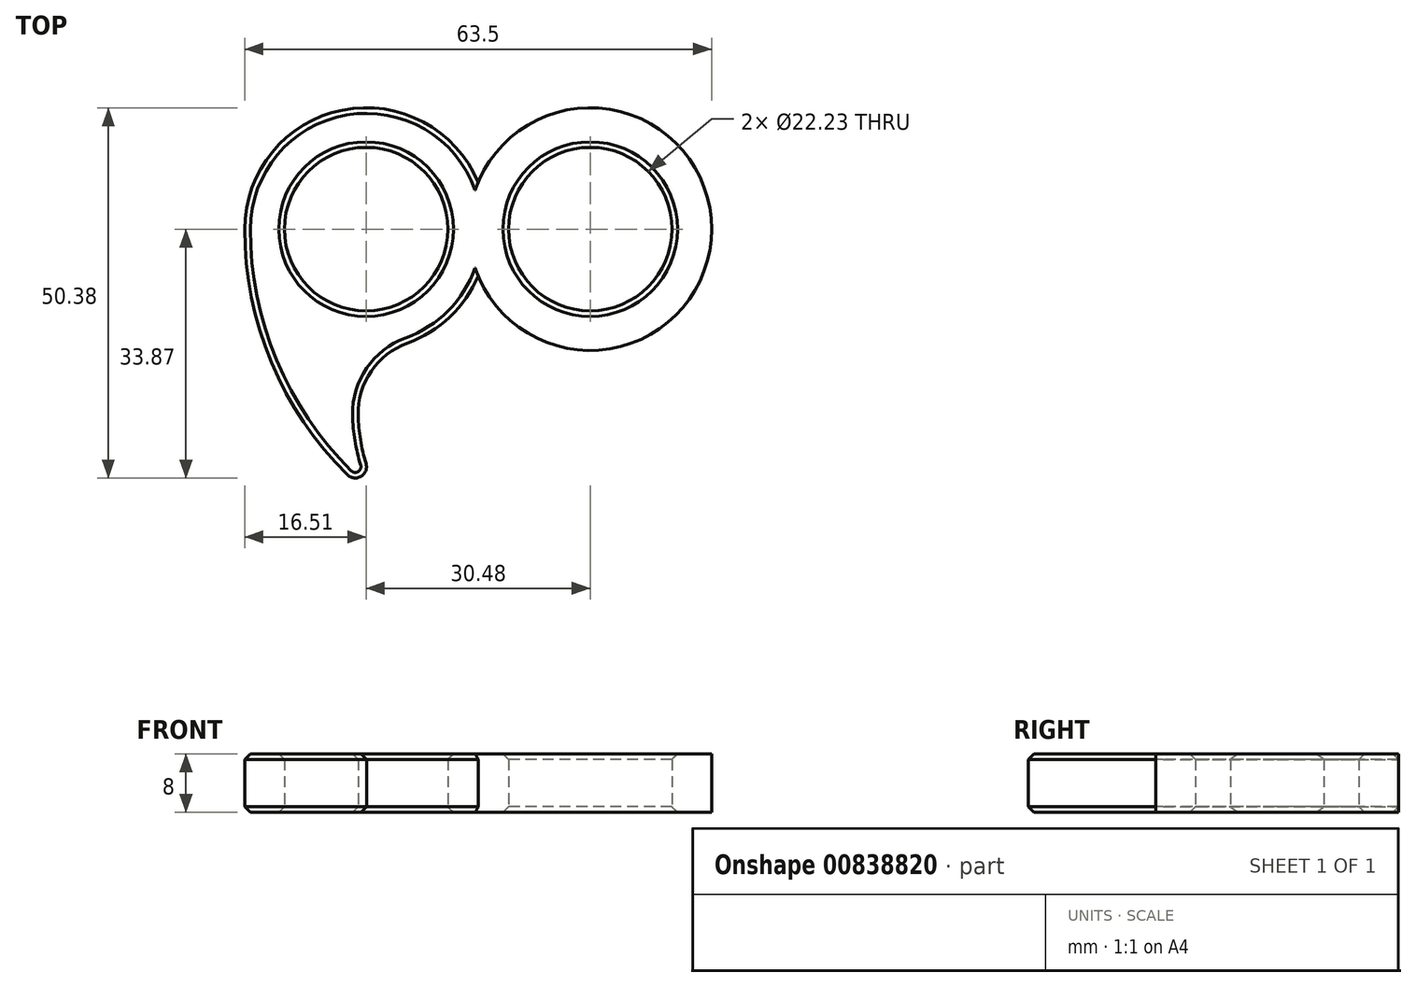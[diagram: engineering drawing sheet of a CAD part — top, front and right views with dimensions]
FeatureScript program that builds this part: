
annotation { "Feature Type Name" : "Feature", "Feature Type Description" : "" }
export const myFeature = defineFeature(function(context is Context, id is Id, definition is map)
    precondition{}
    {
        {
            var Q0;
            Q0=qCreatedBy(makeId("Top.planeOp"),FACE);
            var sketch = newSketch(context, id + "F0", { "sketchPlane" : qUnion([Q0])});
            skCircle(sketch, "E0", {"center": v(0, 0) * mm, "radius": 11.11 * mm});
            skCircle(sketch, "E1", {"center": v(0, 0) * mm, "radius": 16.51 * mm});
            skCircle(sketch, "E2", {"center": v(-30.48, 0) * mm, "radius": 11.11 * mm});
            skCircle(sketch, "E3", {"center": v(-30.48, 0) * mm, "radius": 16.51 * mm});
            skCircle(sketch, "E4", {"center": v(0, 0) * mm, "radius": 47 * mm});
            skArc(sketch, "E5", {"start": v(-30.15, -16.5) * mm, "mid": v(-31.4, -27.53) * mm, "end": v(-27.68, -37.97) * mm});
            skSolve(sketch);
        }
        {
            var Q0;
            Q0=makeQuery(id+"F0.imprint","IMPRINT",FACE,{"disambiguationData":[TD([[makeQuery(id+"F0.imprint","IMPRINT",EDGE,{"derivedFrom":sQuery(id+"F0.wireOp",EDGE,"E0")}),-1.0]])]});
            var Q1;
            {var subQ0=sQuery(id+"F0.wireOp",EDGE,"E3");var subQ1=sQuery(id+"F0.wireOp",EDGE,"E1");var subQ2=makeQuery(id+"F0.imprint","INTERSECT",VERTEX,{"disambiguationData":[OD(0.0)],"derivedFrom":[subQ1,subQ0]});Q1=makeQuery(id+"F0.imprint","IMPRINT",FACE,{"disambiguationData":[TD([[makeQuery(id+"F0.imprint","IMPRINT",EDGE,{"disambiguationData":[TD([[subQ2,-1.0]])],"derivedFrom":subQ1}),1.0]])]});}
            extrude(context, id + "F1", {"entities" : qUnion([Q0, Q1]), "endBound" : BoundingType.SYMMETRIC, "depth" : 8 * mm, "offsetDistance" : 25.4 * mm});
        }
        {
            var Q0;
            Q0=makeQuery(id+"F0.imprint","IMPRINT",FACE,{"disambiguationData":[TD([[makeQuery(id+"F0.imprint","IMPRINT",EDGE,{"derivedFrom":sQuery(id+"F0.wireOp",EDGE,"E2")}),-1.0]])]});
            var Q1;
            {var subQ0=sQuery(id+"F0.wireOp",EDGE,"E5");Q1=makeQuery(id+"F0.imprint","IMPRINT",FACE,{"disambiguationData":[TD([[makeQuery(id+"F0.imprint","IMPRINT",EDGE,{"derivedFrom":subQ0}),-1.0]])]});}
            extrude(context, id + "F2", {"entities" : qUnion([Q0, Q1]), "operationType" : NewBodyOperationType.ADD, "endBound" : BoundingType.SYMMETRIC, "depth" : 8 * mm, "offsetDistance" : 25.4 * mm});
        }
        {
            var Q0;
            {var subQ0=sQuery(id+"F0.wireOp",EDGE,"E3");var subQ1=sQuery(id+"F0.wireOp",EDGE,"E1");Q0=makeQuery(id+"F2.opExtrude","SWEPT_EDGE",EDGE,{"disambiguationData":[OSD([subQ1,subQ0]),TDD([makeQuery(id+"F0.imprint","INTERSECT",VERTEX,{"disambiguationData":[OD(1.0)],"derivedFrom":[subQ1,subQ0]})])]});}
            var Q1;
            {var subQ0=sQuery(id+"F0.wireOp",EDGE,"E3");var subQ1=sQuery(id+"F0.wireOp",EDGE,"E1");Q1=makeQuery(id+"FjYOoVcogSnIJbw_1.1.F2.opExtrude","SWEPT_EDGE",EDGE,{"disambiguationData":[OSD([subQ1,subQ0]),TDD([makeQuery(id+"F0.imprint","INTERSECT",VERTEX,{"disambiguationData":[OD(0.0)],"derivedFrom":[subQ1,subQ0]})])]});}
            var Q2;
            {var subQ0=sQuery(id+"F0.wireOp",EDGE,"E3");var subQ1=sQuery(id+"F0.wireOp",EDGE,"E1");Q2=makeQuery(id+"F2.opExtrude","SWEPT_EDGE",EDGE,{"disambiguationData":[OSD([subQ1,subQ0]),TDD([makeQuery(id+"F0.imprint","INTERSECT",VERTEX,{"disambiguationData":[OD(0.0)],"derivedFrom":[subQ1,subQ0]})])]});}
            var Q3;
            {var subQ0=sQuery(id+"F0.wireOp",EDGE,"E3");var subQ1=sQuery(id+"F0.wireOp",EDGE,"E1");Q3=makeQuery(id+"FjYOoVcogSnIJbw_1.1.F2.opExtrude","SWEPT_EDGE",EDGE,{"disambiguationData":[OSD([subQ1,subQ0]),TDD([makeQuery(id+"F0.imprint","INTERSECT",VERTEX,{"disambiguationData":[OD(1.0)],"derivedFrom":[subQ1,subQ0]})])]});}
            var Q4;
            Q4=makeQuery(id+"F2.opExtrude","SWEPT_EDGE",EDGE,{"disambiguationData":[OSD([sQuery(id+"F0.wireOp",EDGE,"E3"),sQuery(id+"F0.wireOp",EDGE,"E5")])]});
            var Q5;
            Q5=makeQuery(id+"FjYOoVcogSnIJbw_1.1.F2.opExtrude","SWEPT_EDGE",EDGE,{"disambiguationData":[OSD([sQuery(id+"F0.wireOp",EDGE,"E3"),sQuery(id+"F0.wireOp",EDGE,"E5")])]});
            fillet(context, id + "F3", {"entities" : qUnion([Q0, Q1, Q2, Q3, Q4, Q5]), "radius" : 10.16 * mm, "tangentPropagation" : true, "allowEdgeOverflow" : false});
        }
        {
            var Q0;
            Q0=makeQuery(id+"F2.opExtrude","SWEPT_EDGE",EDGE,{"disambiguationData":[OSD([sQuery(id+"F0.wireOp",EDGE,"E4"),sQuery(id+"F0.wireOp",EDGE,"E5")])]});
            var Q1;
            Q1=makeQuery(id+"FjYOoVcogSnIJbw_1.1.F2.opExtrude","SWEPT_EDGE",EDGE,{"disambiguationData":[OSD([sQuery(id+"F0.wireOp",EDGE,"E4"),sQuery(id+"F0.wireOp",EDGE,"E5")])]});
            fillet(context, id + "F4", {"entities" : qUnion([Q0, Q1]), "radius" : 1.52 * mm, "tangentPropagation" : true, "allowEdgeOverflow" : false});
        }
        {
            var Q0;
            {var subQ0=sQuery(id+"F0.wireOp",EDGE,"E5");var subQ1=sQuery(id+"F0.wireOp",EDGE,"E4");var subQ2=sQuery(id+"F0.wireOp",EDGE,"E3");var subQ3=sQuery(id+"F0.wireOp",EDGE,"E2");var subQ4=sQuery(id+"F0.wireOp",EDGE,"E1");Q0=makeQuery(id+"F3.opFillet","BLEND_EDGE",EDGE,{"blendedFrom":[makeQuery(id+"F2.opExtrude","SWEPT_EDGE",EDGE,{"disambiguationData":[OSD([subQ2,subQ0])]}),makeQuery(id+"FjYOoVcogSnIJbw_1.1.F2.boolean.opBoolean","MERGE",FACE,{"derivedFrom":[makeQuery(id+"F2.boolean.opBoolean","MERGE",FACE,{"derivedFrom":[makeQuery(id+"F1.opExtrude","CAP_FACE",FACE,{"disambiguationData":[OSD([sQuery(id+"F0.wireOp",EDGE,"E0"),subQ4])],"isStart":false}),makeQuery(id+"F2.opExtrude","CAP_FACE",FACE,{"disambiguationData":[OSD([subQ4,subQ3,subQ2,subQ1,subQ0])],"isStart":false})]}),makeQuery(id+"FjYOoVcogSnIJbw_1.1.F2.opExtrude","CAP_FACE",FACE,{"disambiguationData":[OSD([subQ4,subQ3,subQ2,subQ1,subQ0])],"isStart":false})]})],"blendedInto":[makeQuery(id+"FjYOoVcogSnIJbw_1.1.F2.boolean.opBoolean","MERGE",FACE,{"derivedFrom":[makeQuery(id+"F2.boolean.opBoolean","MERGE",FACE,{"derivedFrom":[makeQuery(id+"F1.opExtrude","CAP_FACE",FACE,{"disambiguationData":[OSD([sQuery(id+"F0.wireOp",EDGE,"E0"),subQ4])],"isStart":false}),makeQuery(id+"F2.opExtrude","CAP_FACE",FACE,{"disambiguationData":[OSD([subQ4,subQ3,subQ2,subQ1,subQ0])],"isStart":false})]}),makeQuery(id+"FjYOoVcogSnIJbw_1.1.F2.opExtrude","CAP_FACE",FACE,{"disambiguationData":[OSD([subQ4,subQ3,subQ2,subQ1,subQ0])],"isStart":false})]})]});}
            var Q1;
            Q1=makeQuery(id+"F2.opExtrude","CAP_EDGE",EDGE,{"disambiguationData":[OSD([sQuery(id+"F0.wireOp",EDGE,"E4")])],"isStart":true});
            var Q2;
            Q2=makeQuery(id+"F2.opExtrude","CAP_EDGE",EDGE,{"disambiguationData":[OSD([sQuery(id+"F0.wireOp",EDGE,"E2")])],"isStart":false});
            var Q3;
            Q3=makeQuery(id+"F1.opExtrude","CAP_EDGE",EDGE,{"disambiguationData":[OSD([sQuery(id+"F0.wireOp",EDGE,"E0")])],"isStart":false});
            var Q4;
            Q4=makeQuery(id+"FjYOoVcogSnIJbw_1.1.F2.opExtrude","CAP_EDGE",EDGE,{"disambiguationData":[OSD([sQuery(id+"F0.wireOp",EDGE,"E2")])],"isStart":false});
            var Q5;
            Q5=makeQuery(id+"FjYOoVcogSnIJbw_1.1.F2.opExtrude","CAP_EDGE",EDGE,{"disambiguationData":[OSD([sQuery(id+"F0.wireOp",EDGE,"E2")])],"isStart":true});
            var Q6;
            Q6=makeQuery(id+"F1.opExtrude","CAP_EDGE",EDGE,{"disambiguationData":[OSD([sQuery(id+"F0.wireOp",EDGE,"E0")])],"isStart":true});
            var Q7;
            Q7=makeQuery(id+"F2.opExtrude","CAP_EDGE",EDGE,{"disambiguationData":[OSD([sQuery(id+"F0.wireOp",EDGE,"E2")])],"isStart":true});
            chamfer(context, id + "F5", {"entities" : qUnion([Q0, Q1, Q2, Q3, Q4, Q5, Q6, Q7]), "width" : 0.76 * mm, "tangentPropagation" : true});
        }
    });
